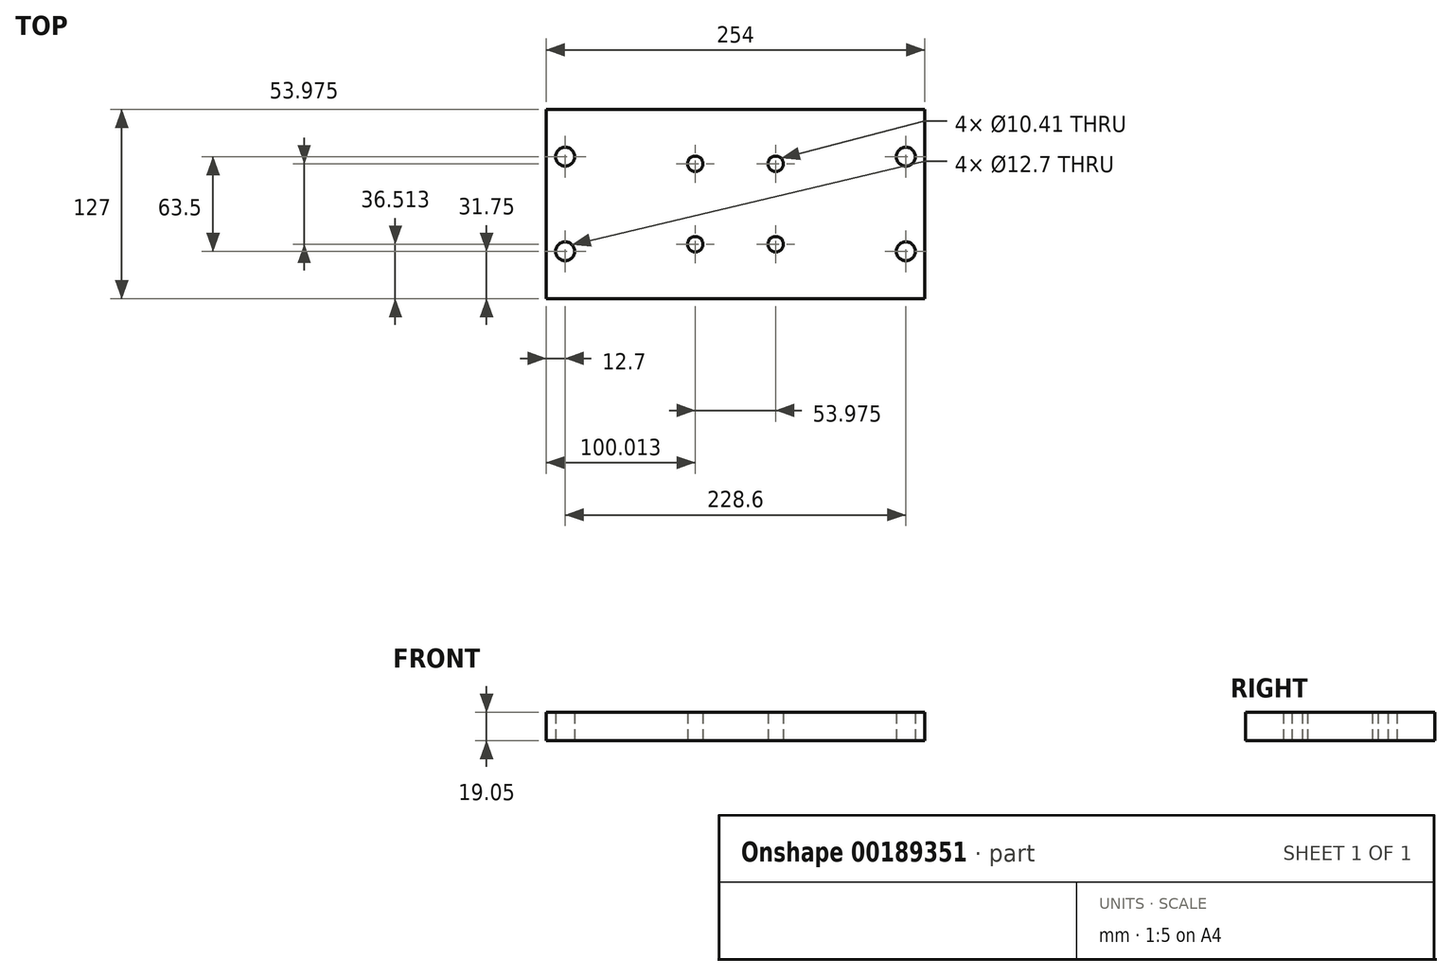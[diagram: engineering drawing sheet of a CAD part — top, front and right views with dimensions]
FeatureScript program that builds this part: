
annotation { "Feature Type Name" : "Feature", "Feature Type Description" : "" }
export const myFeature = defineFeature(function(context is Context, id is Id, definition is map)
    precondition{}
    {
        {
            var Q0;
            Q0=qCreatedBy(makeId("Top.planeOp"),FACE);
            var sketch = newSketch(context, id + "F0", { "sketchPlane" : qUnion([Q0])});
            skLineSegment(sketch, "E0.bottom", {"start": v(-127, 63.5) * mm, "end": v(127, 63.5) * mm});
            skLineSegment(sketch, "E0.top", {"start": v(-127, -63.5) * mm, "end": v(127, -63.5) * mm});
            skLineSegment(sketch, "E0.left", {"start": v(-127, 63.5) * mm, "end": v(-127, -63.5) * mm});
            skLineSegment(sketch, "E0.right", {"start": v(127, 63.5) * mm, "end": v(127, -63.5) * mm});
            skPoint(sketch, "E0.middle", {"position": v(0, 0) * mm});
            skCircle(sketch, "E1", {"center": v(-26.99, 26.99) * mm, "radius": 5.2 * mm});
            skCircle(sketch, "E2.1.0", {"center": v(-26.99, -26.99) * mm, "radius": 5.2 * mm});
            skCircle(sketch, "E2.2.0", {"center": v(26.99, -26.99) * mm, "radius": 5.2 * mm});
            skCircle(sketch, "E2.3.0", {"center": v(26.99, 26.99) * mm, "radius": 5.2 * mm});
            skCircle(sketch, "E3", {"center": v(-114.3, 31.75) * mm, "radius": 6.35 * mm});
            skLineSegment(sketch, "E4", {"start": v(0, 0) * mm, "end": v(21.58, 0) * mm, "construction": true});
            skLineSegment(sketch, "E5", {"start": v(0, 0) * mm, "end": v(0, -21.65) * mm, "construction": true});
            skCircle(sketch, "E6.MirrorC", {"center": v(-114.3, -31.75) * mm, "radius": 6.35 * mm});
            skCircle(sketch, "E7.MirrorC", {"center": v(114.3, 31.75) * mm, "radius": 6.35 * mm});
            skCircle(sketch, "E8.MirrorC", {"center": v(114.3, -31.75) * mm, "radius": 6.35 * mm});
            skSolve(sketch);
        }
        {
            var Q0;
            Q0=makeQuery(id+"F0.imprint","IMPRINT",FACE,{"disambiguationData":[TD([[makeQuery(id+"F0.imprint","IMPRINT",EDGE,{"derivedFrom":sQuery(id+"F0.wireOp",EDGE,"E0.bottom")}),-1.0]])]});
            extrude(context, id + "F1", {"entities" : qUnion([Q0]), "depth" : 19.05 * mm});
        }
    });
